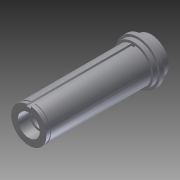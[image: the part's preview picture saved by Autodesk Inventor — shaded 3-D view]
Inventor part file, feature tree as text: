
AUTODESK INVENTOR PART (.ipt)
format: ipt  version: 2012 (Build 160160000, 160)  size: 159,232 bytes
history: native  units: in
note: dims shown in document units (in); Inventor stores cm internally (conversion verified against a paired STEP export)
features: extrude x8, sketch x6, plane x5
ambient origin geometry x8: Origin, YZ Plane, XZ Plane, XY Plane, X Axis, Y Axis, Z Axis, Center Point
feature tree (19):
  sketch  "Sketch1"  dims[d0=1.0in d4=0.5in]
  extrude  "Extrusion4"  Depth=0.5in
  plane  "Work Plane5"
  extrude  "Extrusion8"  [1 undecoded]
  plane  "Work Plane6"
  plane  "Work Plane9"
  plane  "Work Plane10"
  extrude  "Extrusion16"  Depth=0.045in TaperAngle=0.0deg
  extrude  "Extrusion17"  Depth=0.546in
  extrude  "Extrusion18"  Depth=0.125in
  plane  "Work Plane13"
  sketch  "Sketch16"  dims[d50=0.125in d51=0.125in]
  extrude  "Extrusion19"  Depth=0.5625in
  extrude  "Extrusion20"  Depth=0.045in TaperAngle=0.0deg
  extrude  "Extrusion21"  Depth=0.625in
  sketch  "Sketch6"  dims[d9=3.47in d10=0.0in d23=-0.125in]
  sketch  "Sketch14"  dims[d24=0.96in d25=0.045in d26=0.0in]
  sketch  "Sketch15"  dims[d27=-0.595in d36=-1.706in d39=0.546in]
  sketch  "Sketch17"  dims[d52=0.0625in d53=0.5625in d54=0.045in d55=0.0in d56=0.625in d57=0.3125in d58=0.0in d59=0.625in d60=0.3125in d61=0.0in d62=-0.25in d63=1.25in d64=0.125in d65=0.0in d66=0.25in d67=0.0in d68=1.125in d69=0.25in d70=0.0in]
note: 1 required parameter value undecoded (feature->parameter linkage not recoverable at this tier; creation-order binding heuristic only, values carry confidence <= 0.55)
